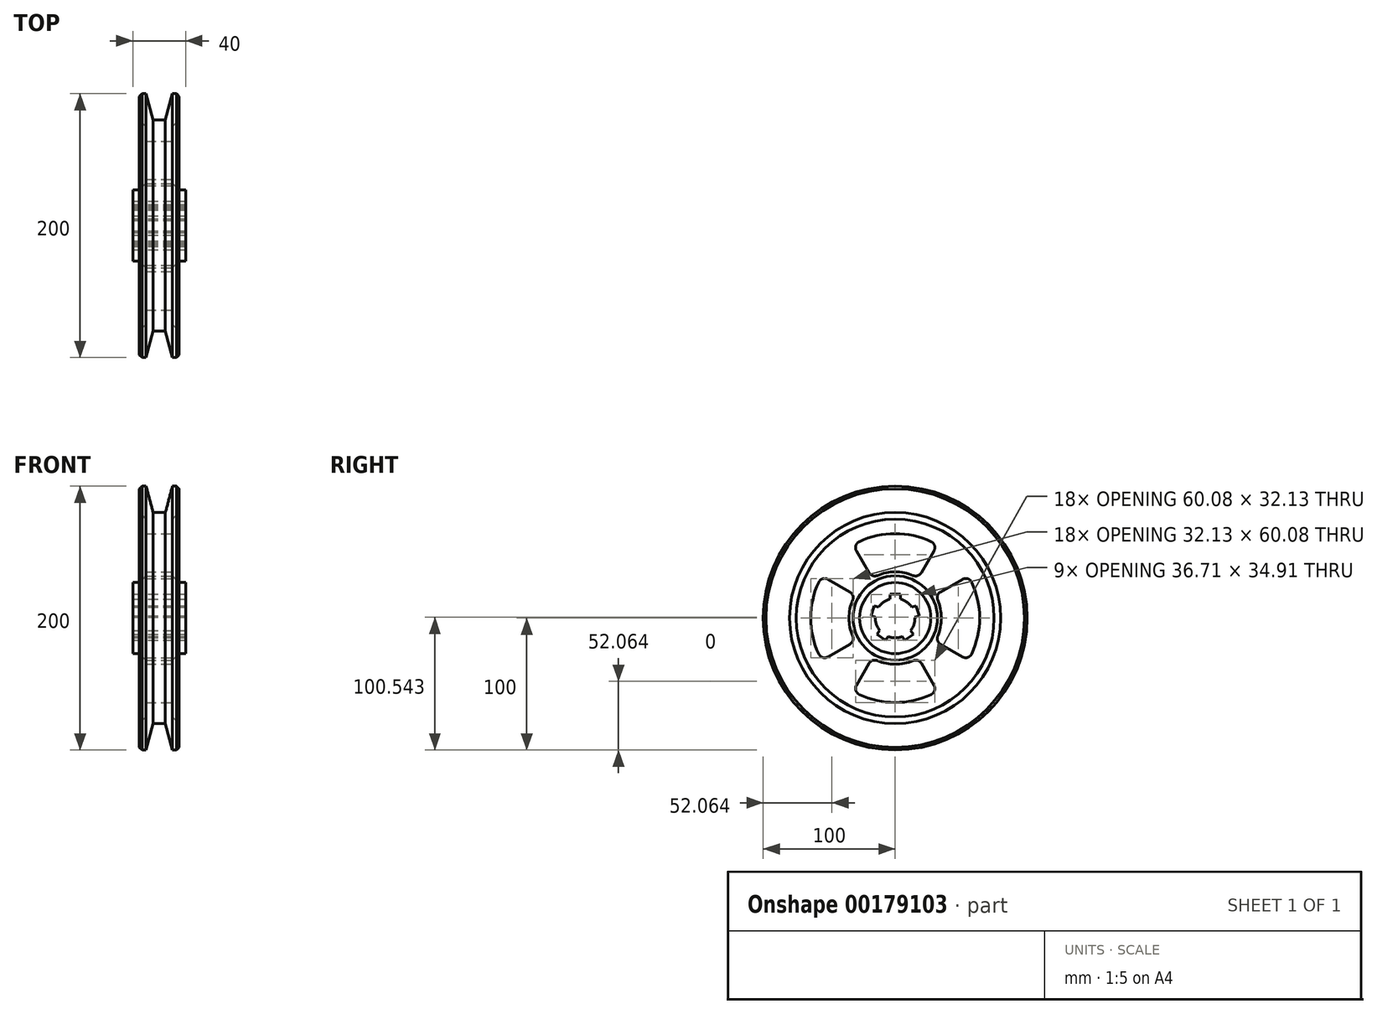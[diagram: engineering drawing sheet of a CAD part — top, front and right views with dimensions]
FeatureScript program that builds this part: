
annotation { "Feature Type Name" : "Feature", "Feature Type Description" : "" }
export const myFeature = defineFeature(function(context is Context, id is Id, definition is map)
    precondition{}
    {
        {
            var Q0;
            Q0=qCreatedBy(makeId("Top.planeOp"),FACE);
            var sketch = newSketch(context, id + "F0", { "sketchPlane" : qUnion([Q0])});
            skLineSegment(sketch, "E0", {"start": v(-20, 0) * mm, "end": v(20, 0) * mm, "construction": true});
            skLineSegment(sketch, "E1", {"start": v(20, 0) * mm, "end": v(20, -27) * mm});
            skLineSegment(sketch, "E2", {"start": v(20, -27) * mm, "end": v(15, -27) * mm});
            skLineSegment(sketch, "E3", {"start": v(15, -27) * mm, "end": v(10, -32) * mm});
            skLineSegment(sketch, "E4", {"start": v(10, -32) * mm, "end": v(10, -75) * mm});
            skLineSegment(sketch, "E5", {"start": v(10, -75) * mm, "end": v(15, -80) * mm});
            skLineSegment(sketch, "E6", {"start": v(15, -80) * mm, "end": v(15, -80) * mm});
            skLineSegment(sketch, "E7", {"start": v(15, -80) * mm, "end": v(15, -98) * mm});
            skLineSegment(sketch, "E8", {"start": v(13, -100) * mm, "end": v(10, -100) * mm});
            skLineSegment(sketch, "E9", {"start": v(10, -100) * mm, "end": v(4.64, -80) * mm});
            skLineSegment(sketch, "E10", {"start": v(4.64, -80) * mm, "end": v(0, -80) * mm});
            skLineSegment(sketch, "E11", {"start": v(15, -98) * mm, "end": v(13, -100) * mm});
            skLineSegment(sketch, "E12", {"start": v(0, 0) * mm, "end": v(0, -121.91) * mm, "construction": true});
            skLineSegment(sketch, "E13", {"start": v(10, -53.5) * mm, "end": v(31.46, -53.5) * mm, "construction": true});
            skLineSegment(sketch, "E14.MirrorCS", {"start": v(-15, -80) * mm, "end": v(-15, -98) * mm});
            skLineSegment(sketch, "E15.MirrorCS", {"start": v(-4.64, -80) * mm, "end": v(0, -80) * mm});
            skLineSegment(sketch, "E16.MirrorCS", {"start": v(-10, -100) * mm, "end": v(-4.64, -80) * mm});
            skLineSegment(sketch, "E17.MirrorCS", {"start": v(-13, -100) * mm, "end": v(-10, -100) * mm});
            skLineSegment(sketch, "E18.MirrorCS", {"start": v(-15, -98) * mm, "end": v(-13, -100) * mm});
            skLineSegment(sketch, "E19.MirrorCS", {"start": v(-10, -75) * mm, "end": v(-15, -80) * mm});
            skLineSegment(sketch, "E20.MirrorCS", {"start": v(-10, -32) * mm, "end": v(-10, -75) * mm});
            skLineSegment(sketch, "E21.MirrorCS", {"start": v(-15, -27) * mm, "end": v(-10, -32) * mm});
            skLineSegment(sketch, "E22.MirrorCS", {"start": v(-20, 0) * mm, "end": v(-20, -27) * mm});
            skLineSegment(sketch, "E23.MirrorCS", {"start": v(-20, -27) * mm, "end": v(-15, -27) * mm});
            skLineSegment(sketch, "E24", {"start": v(-20, 0) * mm, "end": v(20, 0) * mm});
            skSolve(sketch);
        }
        {
            var Q0;
            Q0 = qSketchRegion(id + "F0", true);
            var Q1;
            Q1=sQuery(id+"F0.wireOp",EDGE,"E24");
            revolve(context, id + "F1", {"entities" : qUnion([Q0]), "axis" : qUnion([Q1]), "revolveType" : RevolveType.FULL});
        }
        {
            var Q0;
            Q0=makeQuery(id+"F1.opRevolve","SWEPT_FACE",FACE,{"disambiguationData":[OSD([sQuery(id+"F0.wireOp",EDGE,"E4")])]});
            var sketch = newSketch(context, id + "F2", { "sketchPlane" : qUnion([Q0])});
            skArc(sketch, "E25", {"start": v(27.19, 57.94) * mm, "mid": v(0, 64) * mm, "end": v(-27.19, 57.94) * mm});
            skArc(sketch, "E26", {"start": v(13.57, 32.26) * mm, "mid": v(0, 35) * mm, "end": v(-13.57, 32.26) * mm});
            skLineSegment(sketch, "E27", {"start": v(-19.84, 34.37) * mm, "end": v(-29.4, 50.91) * mm});
            skLineSegment(sketch, "E28", {"start": v(19.84, 34.37) * mm, "end": v(29.4, 50.91) * mm});
            skLineSegment(sketch, "E29", {"start": v(0, 0) * mm, "end": v(115.01, 0) * mm, "construction": true});
            skLineSegment(sketch, "E30", {"start": v(0, -3.51) * mm, "end": v(0, 111.5) * mm, "construction": true});
            skPoint(sketch, "E31.visualSharp", {"position": v(-32, 55.43) * mm});
            skArc(sketch, "E31.filletArc", {"start": v(-27.19, 57.94) * mm, "mid": v(-29.83, 54.9) * mm, "end": v(-29.4, 50.91) * mm});
            skPoint(sketch, "E32.visualSharp", {"position": v(32, 55.43) * mm});
            skArc(sketch, "E32.filletArc", {"start": v(29.4, 50.91) * mm, "mid": v(29.83, 54.9) * mm, "end": v(27.19, 57.94) * mm});
            skPoint(sketch, "E33.visualSharp", {"position": v(-17.5, 30.31) * mm});
            skArc(sketch, "E33.filletArc", {"start": v(-19.84, 34.37) * mm, "mid": v(-17.1, 32.13) * mm, "end": v(-13.57, 32.26) * mm});
            skPoint(sketch, "E34.visualSharp", {"position": v(17.5, 30.31) * mm});
            skArc(sketch, "E34.filletArc", {"start": v(13.57, 32.26) * mm, "mid": v(17.1, 32.13) * mm, "end": v(19.84, 34.37) * mm});
            skArc(sketch, "E35", {"start": v(-4, 14.46) * mm, "mid": v(-8.82, 12.14) * mm, "end": v(-12.51, 8.27) * mm});
            skLineSegment(sketch, "E36", {"start": v(-4, 18) * mm, "end": v(-4, 14.46) * mm});
            skLineSegment(sketch, "E37", {"start": v(4, 14.46) * mm, "end": v(4, 18) * mm});
            skLineSegment(sketch, "E38", {"start": v(4, 18) * mm, "end": v(-4, 18) * mm});
            skLineSegment(sketch, "E39.1.0", {"start": v(-18.36, 1.76) * mm, "end": v(-14.99, 0.66) * mm});
            skLineSegment(sketch, "E39.1.1", {"start": v(-15.88, 9.37) * mm, "end": v(-18.36, 1.76) * mm});
            skLineSegment(sketch, "E39.1.2", {"start": v(-12.51, 8.27) * mm, "end": v(-15.88, 9.37) * mm});
            skLineSegment(sketch, "E39.2.0", {"start": v(-7.34, -16.91) * mm, "end": v(-5.26, -14.05) * mm});
            skLineSegment(sketch, "E39.2.1", {"start": v(-13.82, -12.21) * mm, "end": v(-7.34, -16.91) * mm});
            skLineSegment(sketch, "E39.2.2", {"start": v(-11.73, -9.34) * mm, "end": v(-13.82, -12.21) * mm});
            skLineSegment(sketch, "E39.3.0", {"start": v(13.82, -12.21) * mm, "end": v(11.73, -9.34) * mm});
            skLineSegment(sketch, "E39.3.1", {"start": v(7.34, -16.91) * mm, "end": v(13.82, -12.21) * mm});
            skLineSegment(sketch, "E39.3.2", {"start": v(5.26, -14.05) * mm, "end": v(7.34, -16.91) * mm});
            skLineSegment(sketch, "E39.4.0", {"start": v(15.88, 9.37) * mm, "end": v(12.51, 8.27) * mm});
            skLineSegment(sketch, "E39.4.1", {"start": v(18.36, 1.76) * mm, "end": v(15.88, 9.37) * mm});
            skLineSegment(sketch, "E39.4.2", {"start": v(14.99, 0.66) * mm, "end": v(18.36, 1.76) * mm});
            skArc(sketch, "E40.trimOffspring", {"start": v(-5.26, -14.05) * mm, "mid": v(0, -15) * mm, "end": v(5.26, -14.05) * mm});
            skArc(sketch, "E41.trimOffspring", {"start": v(12.51, 8.27) * mm, "mid": v(8.82, 12.14) * mm, "end": v(4, 14.46) * mm});
            skArc(sketch, "E42.trimOffspring", {"start": v(11.73, -9.34) * mm, "mid": v(14.27, -4.64) * mm, "end": v(14.99, 0.66) * mm});
            skArc(sketch, "E43.trimOffspring", {"start": v(-14.99, 0.66) * mm, "mid": v(-14.27, -4.64) * mm, "end": v(-11.73, -9.34) * mm});
            skArc(sketch, "E44.1.0", {"start": v(-57.94, 27.19) * mm, "mid": v(-64, 0) * mm, "end": v(-57.94, -27.19) * mm});
            skArc(sketch, "E44.1.1", {"start": v(-50.91, 29.4) * mm, "mid": v(-54.9, 29.83) * mm, "end": v(-57.94, 27.19) * mm});
            skLineSegment(sketch, "E44.1.2", {"start": v(-34.37, 19.84) * mm, "end": v(-50.91, 29.4) * mm});
            skArc(sketch, "E44.1.3", {"start": v(-32.26, 13.57) * mm, "mid": v(-32.13, 17.1) * mm, "end": v(-34.37, 19.84) * mm});
            skArc(sketch, "E44.1.4", {"start": v(-32.26, 13.57) * mm, "mid": v(-35, 0) * mm, "end": v(-32.26, -13.57) * mm});
            skArc(sketch, "E44.1.5", {"start": v(-34.37, -19.84) * mm, "mid": v(-32.13, -17.1) * mm, "end": v(-32.26, -13.57) * mm});
            skLineSegment(sketch, "E44.1.6", {"start": v(-34.37, -19.84) * mm, "end": v(-50.91, -29.4) * mm});
            skArc(sketch, "E44.1.7", {"start": v(-57.94, -27.19) * mm, "mid": v(-54.9, -29.83) * mm, "end": v(-50.91, -29.4) * mm});
            skArc(sketch, "E44.2.0", {"start": v(-27.19, -57.94) * mm, "mid": v(0, -64) * mm, "end": v(27.19, -57.94) * mm});
            skArc(sketch, "E44.2.1", {"start": v(-29.4, -50.91) * mm, "mid": v(-29.83, -54.9) * mm, "end": v(-27.19, -57.94) * mm});
            skLineSegment(sketch, "E44.2.2", {"start": v(-19.84, -34.37) * mm, "end": v(-29.4, -50.91) * mm});
            skArc(sketch, "E44.2.3", {"start": v(-13.57, -32.26) * mm, "mid": v(-17.1, -32.13) * mm, "end": v(-19.84, -34.37) * mm});
            skArc(sketch, "E44.2.4", {"start": v(-13.57, -32.26) * mm, "mid": v(0, -35) * mm, "end": v(13.57, -32.26) * mm});
            skArc(sketch, "E44.2.5", {"start": v(19.84, -34.37) * mm, "mid": v(17.1, -32.13) * mm, "end": v(13.57, -32.26) * mm});
            skLineSegment(sketch, "E44.2.6", {"start": v(19.84, -34.37) * mm, "end": v(29.4, -50.91) * mm});
            skArc(sketch, "E44.2.7", {"start": v(27.19, -57.94) * mm, "mid": v(29.83, -54.9) * mm, "end": v(29.4, -50.91) * mm});
            skArc(sketch, "E44.3.0", {"start": v(57.94, -27.19) * mm, "mid": v(64, 0) * mm, "end": v(57.94, 27.19) * mm});
            skArc(sketch, "E44.3.1", {"start": v(50.91, -29.4) * mm, "mid": v(54.9, -29.83) * mm, "end": v(57.94, -27.19) * mm});
            skLineSegment(sketch, "E44.3.2", {"start": v(34.37, -19.84) * mm, "end": v(50.91, -29.4) * mm});
            skArc(sketch, "E44.3.3", {"start": v(32.26, -13.57) * mm, "mid": v(32.13, -17.1) * mm, "end": v(34.37, -19.84) * mm});
            skArc(sketch, "E44.3.4", {"start": v(32.26, -13.57) * mm, "mid": v(35, 0) * mm, "end": v(32.26, 13.57) * mm});
            skArc(sketch, "E44.3.5", {"start": v(34.37, 19.84) * mm, "mid": v(32.13, 17.1) * mm, "end": v(32.26, 13.57) * mm});
            skLineSegment(sketch, "E44.3.6", {"start": v(34.37, 19.84) * mm, "end": v(50.91, 29.4) * mm});
            skArc(sketch, "E44.3.7", {"start": v(57.94, 27.19) * mm, "mid": v(54.9, 29.83) * mm, "end": v(50.91, 29.4) * mm});
            skSolve(sketch);
        }
        {
            var Q0;
            Q0 = qSketchRegion(id + "F2", true);
            extrude(context, id + "F3", {"entities" : qUnion([Q0]), "operationType" : NewBodyOperationType.REMOVE, "endBound" : BoundingType.SYMMETRIC, "oppositeDirection" : true, "depth" : 140 * mm});
        }
    });
